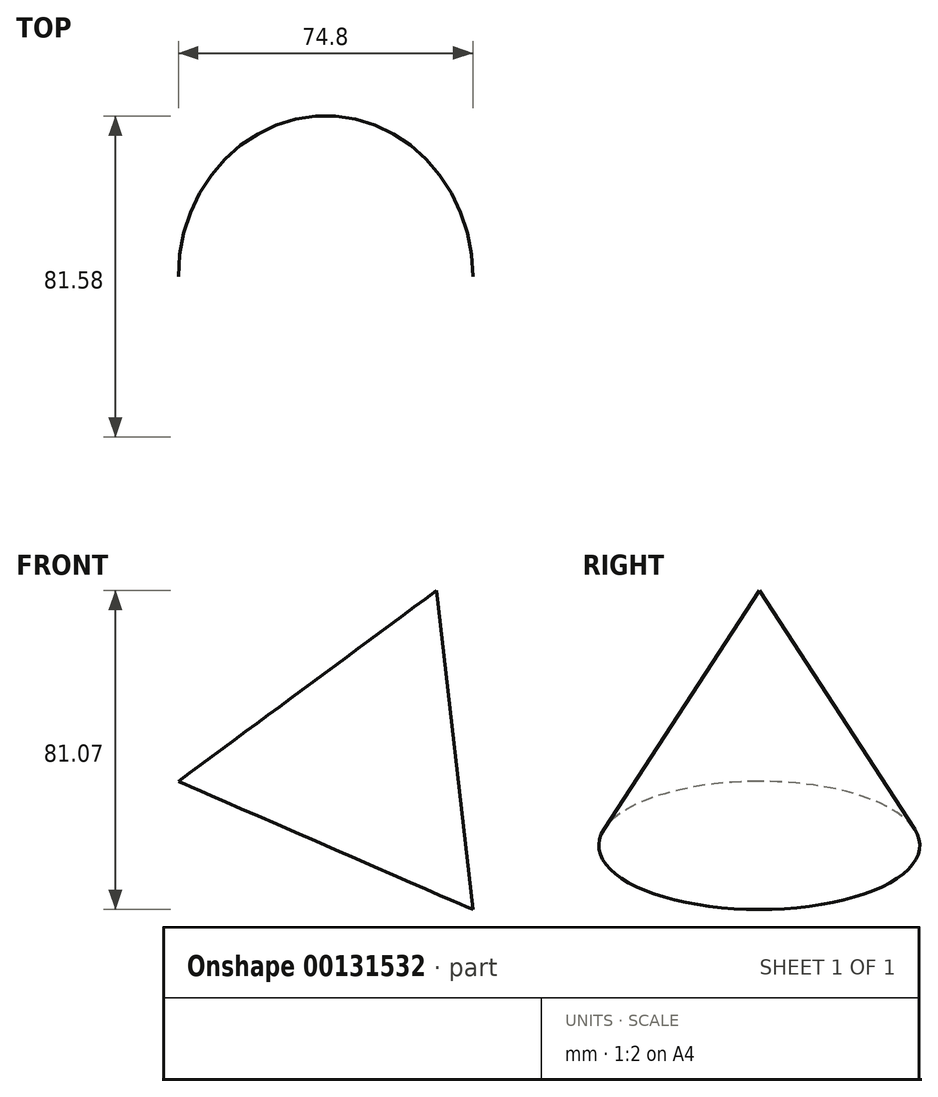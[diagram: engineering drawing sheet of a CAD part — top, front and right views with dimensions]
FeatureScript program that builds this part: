
annotation { "Feature Type Name" : "Feature", "Feature Type Description" : "" }
export const myFeature = defineFeature(function(context is Context, id is Id, definition is map)
    precondition{}
    {
        {
            var Q0;
            Q0=qCreatedBy(makeId("Front.planeOp"),FACE);
            var sketch = newSketch(context, id + "F0", { "sketchPlane" : qUnion([Q0])});
            skCircle(sketch, "E0.cCircle", {"center": v(0, 0) * mm, "radius": 47.1 * mm, "construction": true});
            skLineSegment(sketch, "E0.0", {"start": v(18.8, 43.19) * mm, "end": v(28, -37.88) * mm});
            skLineSegment(sketch, "E0.1", {"start": v(28, -37.88) * mm, "end": v(-46.8, -5.3) * mm});
            skLineSegment(sketch, "E0.2", {"start": v(-46.8, -5.3) * mm, "end": v(18.8, 43.19) * mm});
            skLineSegment(sketch, "E1", {"start": v(18.8, 43.19) * mm, "end": v(-18.8, -43.19) * mm});
            skSolve(sketch);
        }
        {
            var Q0;
            {var subQ0=sQuery(id+"F0.wireOp",EDGE,"E0.0");Q0=makeQuery(id+"F0.imprint","IMPRINT",FACE,{"disambiguationData":[TD([[makeQuery(id+"F0.imprint","IMPRINT",EDGE,{"derivedFrom":subQ0}),-1.0]])]});}
            var Q1;
            Q1=sQuery(id+"F0.wireOp",EDGE,"E1");
            revolve(context, id + "F1", {"entities" : qUnion([Q0]), "axis" : qUnion([Q1]), "revolveType" : RevolveType.FULL});
        }
    });
